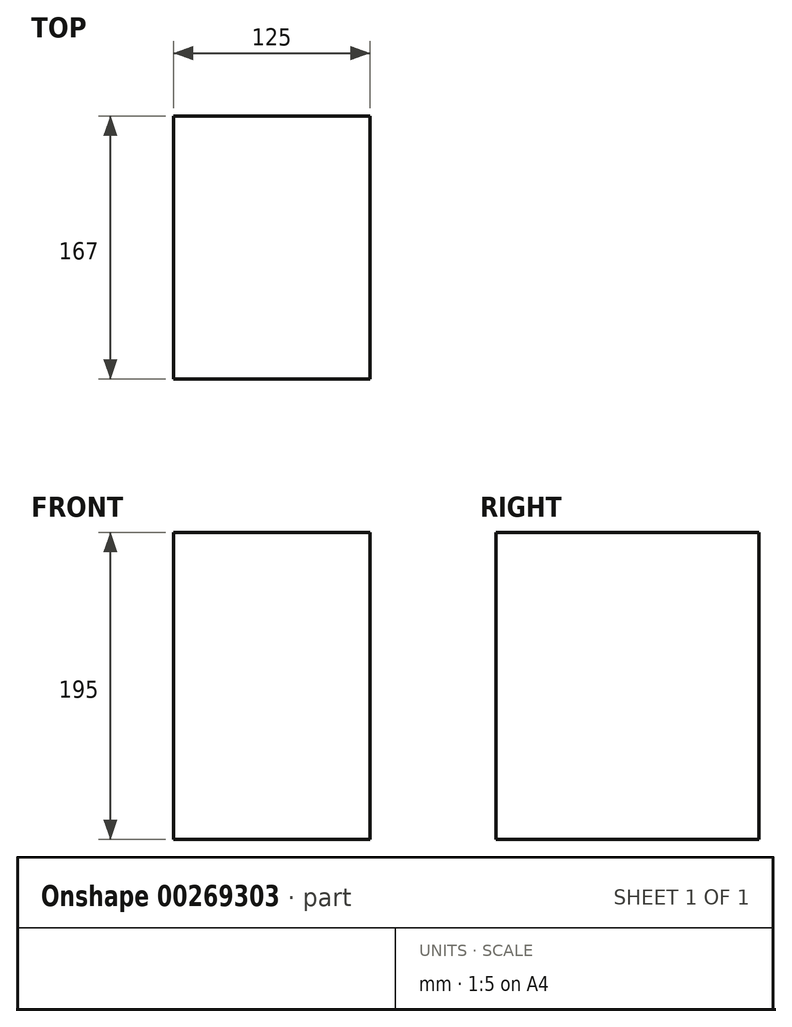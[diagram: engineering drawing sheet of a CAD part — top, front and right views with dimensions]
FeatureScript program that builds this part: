
annotation { "Feature Type Name" : "Feature", "Feature Type Description" : "" }
export const myFeature = defineFeature(function(context is Context, id is Id, definition is map)
    precondition{}
    {
        {
            var Q0;
            Q0=qCreatedBy(makeId("Top.planeOp"),FACE);
            var sketch = newSketch(context, id + "F0", { "sketchPlane" : qUnion([Q0])});
            skLineSegment(sketch, "E0.bottom", {"start": v(-62.5, 83.5) * mm, "end": v(62.5, 83.5) * mm});
            skLineSegment(sketch, "E0.top", {"start": v(-62.5, -83.5) * mm, "end": v(62.5, -83.5) * mm});
            skLineSegment(sketch, "E0.left", {"start": v(-62.5, 83.5) * mm, "end": v(-62.5, -83.5) * mm});
            skLineSegment(sketch, "E0.right", {"start": v(62.5, 83.5) * mm, "end": v(62.5, -83.5) * mm});
            skPoint(sketch, "E0.middle", {"position": v(0, 0) * mm});
            skSolve(sketch);
        }
        {
            var Q0;
            Q0 = qSketchRegion(id + "F0", true);
            extrude(context, id + "F1", {"entities" : qUnion([Q0]), "depth" : 195 * mm});
        }
    });
